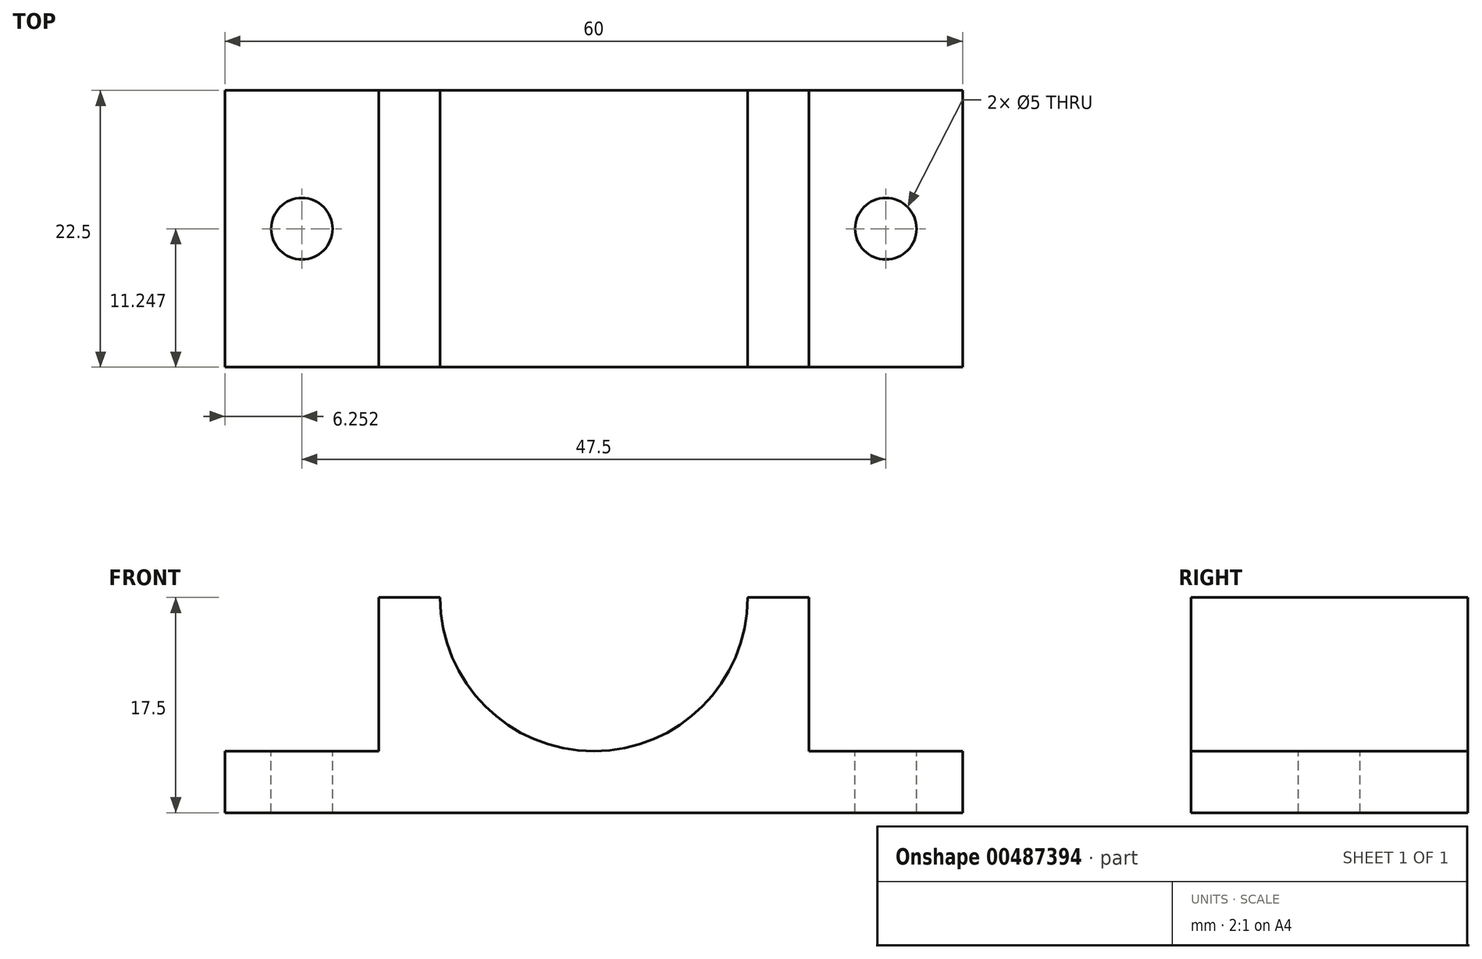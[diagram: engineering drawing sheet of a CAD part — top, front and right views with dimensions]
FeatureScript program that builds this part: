
annotation { "Feature Type Name" : "Feature", "Feature Type Description" : "" }
export const myFeature = defineFeature(function(context is Context, id is Id, definition is map)
    precondition{}
    {
        {
            var Q0;
            Q0=qCreatedBy(makeId("Top.planeOp"),FACE);
            var sketch = newSketch(context, id + "F0", { "sketchPlane" : qUnion([Q0])});
            skLineSegment(sketch, "E0.bottom", {"start": v(-31.89, -2.6) * mm, "end": v(28.11, -2.6) * mm});
            skLineSegment(sketch, "E0.top", {"start": v(-31.89, -25.1) * mm, "end": v(28.11, -25.1) * mm});
            skLineSegment(sketch, "E0.left", {"start": v(-31.89, -2.6) * mm, "end": v(-31.89, -25.1) * mm});
            skLineSegment(sketch, "E0.right", {"start": v(28.11, -2.6) * mm, "end": v(28.11, -25.1) * mm});
            skSolve(sketch);
        }
        {
            var Q0;
            Q0 = qSketchRegion(id + "F0", true);
            extrude(context, id + "F1", {"entities" : qUnion([Q0]), "depth" : 17.5 * mm});
        }
        {
            var Q0;
            Q0=makeQuery(id+"F1.opExtrude","SWEPT_FACE",FACE,{"disambiguationData":[OSD([sQuery(id+"F0.wireOp",EDGE,"E0.top")])]});
            var sketch = newSketch(context, id + "F2", { "sketchPlane" : qUnion([Q0])});
            skLineSegment(sketch, "E1", {"start": v(15.61, 17.5) * mm, "end": v(15.61, 5) * mm});
            skLineSegment(sketch, "E2", {"start": v(15.61, 5) * mm, "end": v(28.11, 5) * mm});
            skLineSegment(sketch, "E3", {"start": v(-19.39, 17.5) * mm, "end": v(-19.39, 5) * mm});
            skLineSegment(sketch, "E4", {"start": v(-19.39, 5) * mm, "end": v(-31.89, 5) * mm});
            skArc(sketch, "E5", {"start": v(-14.39, 17.5) * mm, "mid": v(-1.89, 5) * mm, "end": v(10.61, 17.5) * mm});
            skLineSegment(sketch, "E6", {"start": v(-14.39, 17.5) * mm, "end": v(-19.39, 17.5) * mm});
            skLineSegment(sketch, "E7", {"start": v(10.61, 17.5) * mm, "end": v(15.61, 17.5) * mm});
            skLineSegment(sketch, "E8", {"start": v(-31.89, 5) * mm, "end": v(-31.89, 0) * mm});
            skLineSegment(sketch, "E9", {"start": v(28.11, 5) * mm, "end": v(28.11, 0) * mm});
            skSolve(sketch);
        }
        {
            var Q0;
            {var subQ0=sQuery(id+"F2.wireOp",EDGE,"E3");Q0=makeQuery(id+"F2.imprint","IMPRINT",FACE,{"disambiguationData":[TD([[makeQuery(id+"F2.imprint","IMPRINT",EDGE,{"derivedFrom":subQ0}),-1.0]])]});}
            var Q1;
            {var subQ0=sQuery(id+"F2.wireOp",EDGE,"E5");Q1=makeQuery(id+"F2.imprint","IMPRINT",FACE,{"disambiguationData":[TD([[makeQuery(id+"F2.imprint","IMPRINT",EDGE,{"derivedFrom":subQ0}),1.0]])]});}
            var Q2;
            {var subQ0=sQuery(id+"F2.wireOp",EDGE,"E1");Q2=makeQuery(id+"F2.imprint","IMPRINT",FACE,{"disambiguationData":[TD([[makeQuery(id+"F2.imprint","IMPRINT",EDGE,{"derivedFrom":subQ0}),1.0]])]});}
            extrude(context, id + "F3", {"entities" : qUnion([Q0, Q1, Q2]), "operationType" : NewBodyOperationType.REMOVE, "endBound" : BoundingType.THROUGH_ALL, "oppositeDirection" : true, "depth" : 25 * mm});
        }
        {
            var Q0;
            Q0=makeQuery(id+"F3.boolean.opBoolean","COPY",FACE,{"derivedFrom":makeQuery(id+"F3.opExtrude","SWEPT_FACE",FACE,{"disambiguationData":[OSD([sQuery(id+"F2.wireOp",EDGE,"E2")])]})});
            var sketch = newSketch(context, id + "F4", { "sketchPlane" : qUnion([Q0])});
            skCircle(sketch, "E10", {"center": v(21.86, -13.85) * mm, "radius": 2.5 * mm});
            skPoint(sketch, "E10.centerSnap0", {"position": v(28.11, -13.85) * mm});
            skPoint(sketch, "E10.centerSnap1", {"position": v(21.86, -2.6) * mm});
            skSolve(sketch);
        }
        {
            var Q0;
            Q0=makeQuery(id+"F4.imprint","IMPRINT",FACE,{"disambiguationData":[TD([[makeQuery(id+"F4.imprint","IMPRINT",EDGE,{"derivedFrom":sQuery(id+"F4.wireOp",EDGE,"E10")}),1.0]])]});
            extrude(context, id + "F5", {"entities" : qUnion([Q0]), "operationType" : NewBodyOperationType.REMOVE, "endBound" : BoundingType.THROUGH_ALL, "oppositeDirection" : true, "depth" : 25 * mm});
        }
        {
            var Q0;
            Q0=makeQuery(id+"F3.boolean.opBoolean","COPY",FACE,{"derivedFrom":makeQuery(id+"F3.opExtrude","SWEPT_FACE",FACE,{"disambiguationData":[OSD([sQuery(id+"F2.wireOp",EDGE,"E4")])]})});
            var sketch = newSketch(context, id + "F6", { "sketchPlane" : qUnion([Q0])});
            skCircle(sketch, "E11", {"center": v(-25.64, -13.85) * mm, "radius": 2.5 * mm});
            skPoint(sketch, "E11.centerSnap0", {"position": v(-31.89, -13.85) * mm});
            skPoint(sketch, "E11.centerSnap1", {"position": v(-25.64, -25.1) * mm});
            skSolve(sketch);
        }
        {
            var Q0;
            Q0 = qSketchRegion(id + "F6", true);
            extrude(context, id + "F7", {"entities" : qUnion([Q0]), "operationType" : NewBodyOperationType.REMOVE, "endBound" : BoundingType.THROUGH_ALL, "oppositeDirection" : true, "depth" : 25 * mm});
        }
    });
